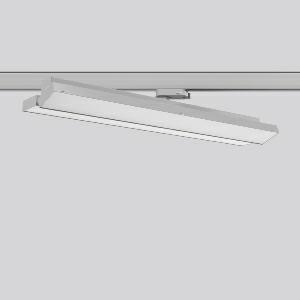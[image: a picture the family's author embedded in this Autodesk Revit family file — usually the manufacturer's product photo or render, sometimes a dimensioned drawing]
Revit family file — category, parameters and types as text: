
# Revit family: tx-move_742164_004_1_76_e766
name_source: partatom
category: Lighting Fixtures
units: mm (PartAtom-declared; Revit-internal decimal feet)

## family parameters
Cut with Voids When Loaded = No
Host = Face
Light Source = No
Part Type = Normal
Room Calculation Point = No
Round Connector Dimension = Use Diameter
Shared = No

## types (1)
- MultiLumen 1 (1 x LED Modul 840, 2625 lm, 4000)
    Apparent Load = 41 VA
    CIE Flux Codes = 47 79 96 100 100
    Color Rendering = 80
    Color Temperature = 4000
    Default Elevation = 1800 mm
    Description = Series: TX-MOVE
Multifunctional surface-mounted spotlight for area lighting. Very flat design. Housing: sheet steel, powder-coated. Rotation range: 356°. Swivel range: 90°. Consistent alignment possible with visible tilt scale. High-efficiency LED units with flush-mounted opal diffuser made of non-yellowing PMMA. Symmetrical wide beam light emission. With adapter for RZB 3-circuit DALI tracks. Suitable for Track on ceiling. MultiLumen: Luminous flux adjustable in 3 steps. Factory setting is the highest luminous flux. Environmentally friendly and resource-saving due to replaceable and recyclable components. 
Colour: silver, matt (approx. RAL 9006)
Length: 570 mm
Width: 119 mm
Height: 88 mm
Lamp: LED
Socket: without socket
Colour temperature: 4000K
Colour rendering index (CRI): 80
System power: 41 W
Rated luminous flux: 5250 lm
Luminous efficiency: 128 lm/W
System power 2: 57 W
Rated luminous flux 2: 7150 lm
Luminous efficiency 2: 125 lm/W
System power 3: 73 W
Rated luminous flux 3: 8750 lm
Luminous efficiency 3: 120 lm/W
Control gear: Dimmable EVG, DALI
Protection class: I
Type of protection: IP 20
    Height = 75 mm
    Lamp = 1 x LED Modul 840
    Lamp Light Flux = 2625 lm
    Lamp count = 1
    Length = 569 mm
    Lifetime = 50000 h
    Luminous efficacy = 128 lm/W
    Manufacturer = RZB
    ModVariant = No
    Model = 742164.004.1.76
    Mounting Place = Ceiling
    Mounting Type = Surface mounted
    Number of Poles = 1
    OnlyDefault = Yes
    Power Factor = 1
    Product Name = TX-MOVE
    Product group = Track mounted projectors
    ProductGroupID = 301
    Protection Class = Protection class I
    Protection Degree = IP 20
    RLX_Detail_Level = 1
    RLX_Emergency_Light_Flux = 0 lm
    RLX_Emergency_Type = 0
    RLX_Emergency_Type_DB = No
    RlxData = <blob elided: 32353 chars, md5=8c14a191>
    Socket = socket
    Standby Power = 0 W
    System Light Flux = 5250 lm
    System Power = 41 W
    Type Comments = MultiLumen 1
    Type Image = 742164.004.jpg
    URL = http://relux.com
    VarID = multilumen_1
    Voltage = 0 V
    Weight = 0.00 kg
    Width = 119 mm

## geometry (parser evidence)
native form markers: Blend x4, Sweep x15
no freeform markers — native parametric forms only
